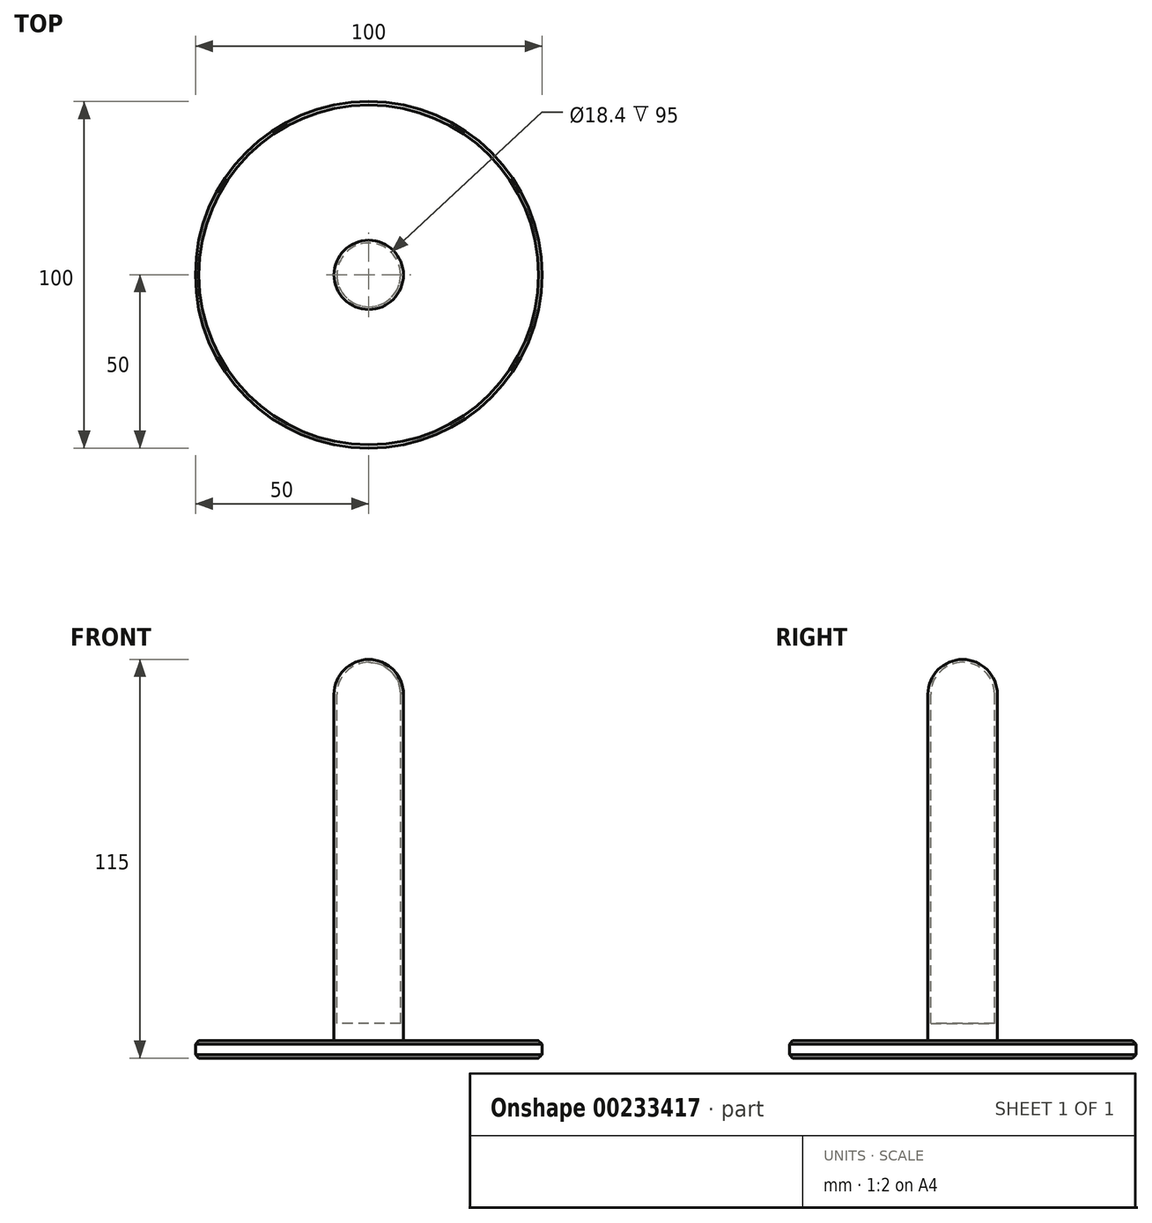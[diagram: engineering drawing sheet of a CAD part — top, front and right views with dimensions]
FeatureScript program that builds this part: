
annotation { "Feature Type Name" : "Feature", "Feature Type Description" : "" }
export const myFeature = defineFeature(function(context is Context, id is Id, definition is map)
    precondition{}
    {
        {
            var Q0;
            Q0=qCreatedBy(makeId("Top.planeOp"),FACE);
            var sketch = newSketch(context, id + "F0", { "sketchPlane" : qUnion([Q0])});
            skCircle(sketch, "E0", {"center": v(0, 0) * mm, "radius": 50 * mm});
            skSolve(sketch);
        }
        {
            var Q0;
            Q0 = qSketchRegion(id + "F0", true);
            extrude(context, id + "F1", {"entities" : qUnion([Q0]), "depth" : 5 * mm, "offsetDistance" : 25 * mm});
        }
        {
            var Q0;
            Q0=makeQuery(id+"F1.opExtrude","CAP_FACE",FACE,{"disambiguationData":[OSD([sQuery(id+"F0.wireOp",EDGE,"E0")])],"isStart":false});
            var sketch = newSketch(context, id + "F2", { "sketchPlane" : qUnion([Q0])});
            skCircle(sketch, "E1", {"center": v(0, 0) * mm, "radius": 10 * mm});
            skSolve(sketch);
        }
        {
            var Q0;
            Q0 = qSketchRegion(id + "F2", true);
            extrude(context, id + "F3", {"entities" : qUnion([Q0]), "operationType" : NewBodyOperationType.ADD, "depth" : 100 * mm, "offsetDistance" : 25 * mm});
        }
        {
            var Q0;
            Q0=makeQuery(id+"F3.opExtrude","CAP_FACE",FACE,{"disambiguationData":[OSD([sQuery(id+"F2.wireOp",EDGE,"E1")])],"isStart":false});
            var sketch = newSketch(context, id + "F4", { "sketchPlane" : qUnion([Q0])});
            skCircle(sketch, "E2", {"center": v(0, 0) * mm, "radius": 9.2 * mm});
            skSolve(sketch);
        }
        {
            var Q0;
            Q0=makeQuery(id+"F4.imprint","IMPRINT",FACE,{"disambiguationData":[TD([[makeQuery(id+"F4.imprint","IMPRINT",EDGE,{"derivedFrom":sQuery(id+"F4.wireOp",EDGE,"E2")}),1.0]])]});
            var Q1;
            Q1=makeQuery(id+"F1.opExtrude","CAP_FACE",FACE,{"disambiguationData":[OSD([sQuery(id+"F0.wireOp",EDGE,"E0")])],"isStart":false});
            extrude(context, id + "F5", {"entities" : qUnion([Q0]), "operationType" : NewBodyOperationType.REMOVE, "endBound" : BoundingType.UP_TO_SURFACE, "oppositeDirection" : true, "depth" : 25 * mm, "endBoundEntityFace" : qUnion([Q1]), "hasOffset" : true, "offsetDistance" : 5 * mm});
        }
        {
            var Q0;
            Q0=makeQuery(id+"F1.opExtrude","CAP_EDGE",EDGE,{"disambiguationData":[OSD([sQuery(id+"F0.wireOp",EDGE,"E0")])],"isStart":false});
            var Q1;
            Q1=makeQuery(id+"F1.opExtrude","CAP_EDGE",EDGE,{"disambiguationData":[OSD([sQuery(id+"F0.wireOp",EDGE,"E0")])],"isStart":true});
            chamfer(context, id + "F6", {"entities" : qUnion([Q0, Q1]), "width" : 1 * mm, "tangentPropagation" : true});
        }
        {
            var Q0;
            Q0=qCreatedBy(makeId("Front.planeOp"),FACE);
            var sketch = newSketch(context, id + "F7", { "sketchPlane" : qUnion([Q0])});
            skLineSegment(sketch, "E3", {"start": v(0, 105) * mm, "end": v(0, 114.2) * mm, "construction": true});
            skArc(sketch, "E4", {"start": v(10, 105) * mm, "mid": v(7.07, 112.07) * mm, "end": v(0, 115) * mm});
            skArc(sketch, "E5", {"start": v(9.2, 105) * mm, "mid": v(6.5, 111.5) * mm, "end": v(0, 114.2) * mm});
            skLineSegment(sketch, "E6", {"start": v(9.2, 105) * mm, "end": v(8.25, 106.27) * mm, "construction": true});
            skLineSegment(sketch, "E7", {"start": v(0, 115) * mm, "end": v(0, 114.2) * mm});
            skLineSegment(sketch, "E8.trimOffspring", {"start": v(0, 114.2) * mm, "end": v(0, 115) * mm, "construction": true});
            skLineSegment(sketch, "E9.trimOffspring", {"start": v(9.2, 105) * mm, "end": v(10, 105) * mm});
            skPoint(sketch, "E10.orphan", {"position": v(-10, 105) * mm});
            skSolve(sketch);
        }
        {
            var Q0;
            Q0=makeQuery(id+"F7.imprint","IMPRINT",FACE,{"disambiguationData":[TD([[makeQuery(id+"F7.imprint","IMPRINT",EDGE,{"derivedFrom":sQuery(id+"F7.wireOp",EDGE,"E4")}),1.0]])]});
            var Q1;
            Q1=sQuery(id+"F7.wireOp",EDGE,"E3");
            revolve(context, id + "F8", {"operationType" : NewBodyOperationType.ADD, "surfaceOperationType" : NewSurfaceOperationType.NEW, "entities" : qUnion([Q0]), "axis" : qUnion([Q1]), "revolveType" : RevolveType.FULL});
        }
    });
